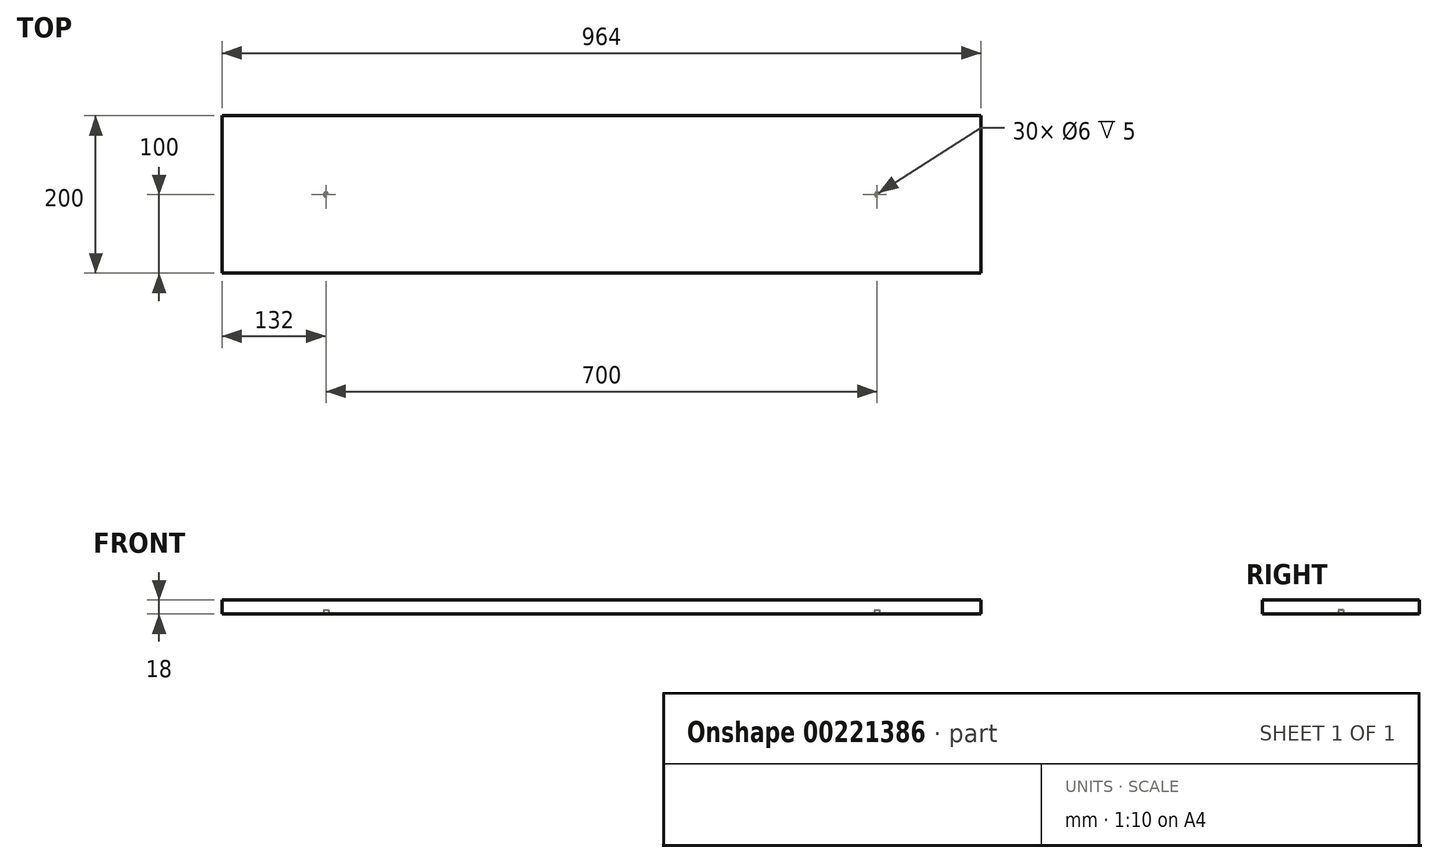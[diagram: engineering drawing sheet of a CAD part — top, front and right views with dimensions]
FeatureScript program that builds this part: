
annotation { "Feature Type Name" : "Feature", "Feature Type Description" : "" }
export const myFeature = defineFeature(function(context is Context, id is Id, definition is map)
    precondition{}
    {
        {
            var Q0;
            Q0=qCreatedBy(makeId("Top.planeOp"),FACE);
            var sketch = newSketch(context, id + "F0", { "sketchPlane" : qUnion([Q0])});
            skLineSegment(sketch, "E0.bottom", {"start": v(482, -100) * mm, "end": v(-482, -100) * mm});
            skLineSegment(sketch, "E0.top", {"start": v(482, 100) * mm, "end": v(-482, 100) * mm});
            skLineSegment(sketch, "E0.left", {"start": v(482, -100) * mm, "end": v(482, 100) * mm});
            skLineSegment(sketch, "E0.right", {"start": v(-482, -100) * mm, "end": v(-482, 100) * mm});
            skPoint(sketch, "E0.middle", {"position": v(0, 0) * mm});
            skSolve(sketch);
        }
        {
            var Q0;
            Q0=qSketchRegion(id+"F0",true);
            extrude(context, id + "F1", {"entities" : qUnion([Q0]), "depth" : 18 * mm});
        }
        {
            var Q0;
            Q0=makeQuery(id+"F1.opExtrude","CAP_FACE",FACE,{"disambiguationData":[OSD([sQuery(id+"F0.wireOp",EDGE,"E0.bottom"),sQuery(id+"F0.wireOp",EDGE,"E0.top"),sQuery(id+"F0.wireOp",EDGE,"E0.left"),sQuery(id+"F0.wireOp",EDGE,"E0.right")])],"isStart":true});
            var sketch = newSketch(context, id + "F2", { "sketchPlane" : qUnion([Q0])});
            skCircle(sketch, "E1", {"center": v(-350, 0) * mm, "radius": 3 * mm});
            skCircle(sketch, "E2", {"center": v(350, 0) * mm, "radius": 3 * mm});
            skSolve(sketch);
        }
        {
            var Q0;
            Q0=qSketchRegion(id+"F2",true);
            extrude(context, id + "F3", {"entities" : qUnion([Q0]), "operationType" : NewBodyOperationType.REMOVE, "oppositeDirection" : true, "depth" : 5 * mm});
        }
    });
